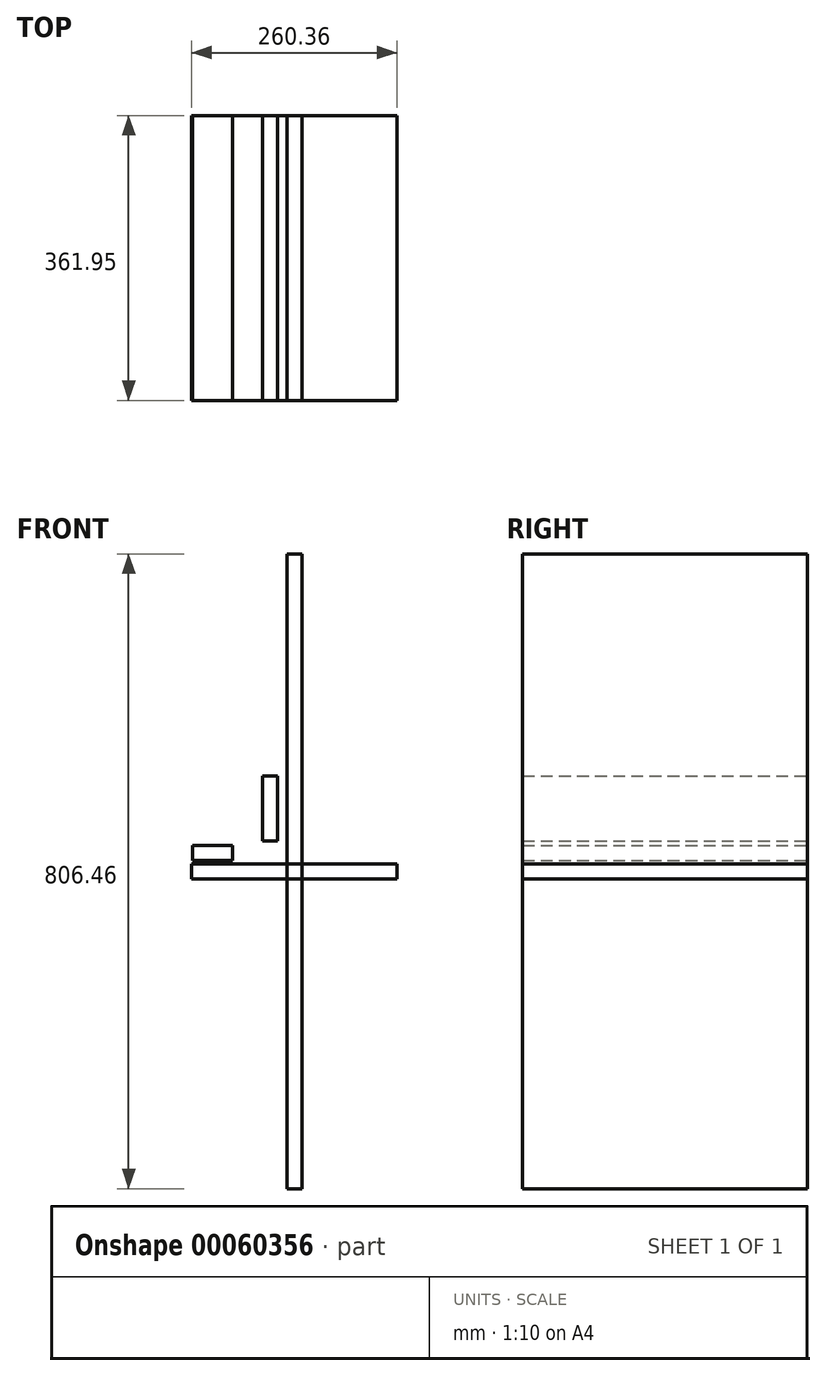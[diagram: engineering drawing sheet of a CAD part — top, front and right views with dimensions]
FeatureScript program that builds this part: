
annotation { "Feature Type Name" : "Feature", "Feature Type Description" : "" }
export const myFeature = defineFeature(function(context is Context, id is Id, definition is map)
    precondition{}
    {
        {
            var Q0;
            Q0=qCreatedBy(makeId("Front.planeOp"),FACE);
            var sketch = newSketch(context, id + "F0", { "sketchPlane" : qUnion([Q0])});
            skLineSegment(sketch, "E0.rect.bottom", {"start": v(9.52, -403.23) * mm, "end": v(-9.53, -403.23) * mm});
            skLineSegment(sketch, "E0.rect.top", {"start": v(9.53, 403.23) * mm, "end": v(-9.52, 403.23) * mm});
            skLineSegment(sketch, "E0.rect.left", {"start": v(9.52, -403.23) * mm, "end": v(9.53, 403.23) * mm});
            skLineSegment(sketch, "E0.rect.right", {"start": v(-9.53, -403.23) * mm, "end": v(-9.52, 403.23) * mm});
            skPoint(sketch, "E0.rect.middle", {"position": v(0, 0) * mm});
            skSolve(sketch);
        }
        {
            var Q0;
            Q0=makeQuery(id+"F0.imprint","IMPRINT",FACE,{"disambiguationData":[TD([[makeQuery(id+"F0.imprint","IMPRINT",EDGE,{"derivedFrom":sQuery(id+"F0.wireOp",EDGE,"E0.rect.bottom")}),-1.0]])]});
            extrude(context, id + "F1", {"entities" : qUnion([Q0]), "depth" : 361.95 * mm});
        }
        {
            var Q0;
            Q0=qCreatedBy(makeId("Front.planeOp"),FACE);
            var sketch = newSketch(context, id + "F2", { "sketchPlane" : qUnion([Q0])});
            skLineSegment(sketch, "E1.rect.bottom", {"start": v(130.18, -9.53) * mm, "end": v(-130.18, -9.53) * mm});
            skLineSegment(sketch, "E1.rect.top", {"start": v(130.18, 9.53) * mm, "end": v(-130.18, 9.53) * mm});
            skLineSegment(sketch, "E1.rect.left", {"start": v(130.18, -9.53) * mm, "end": v(130.18, 9.52) * mm});
            skLineSegment(sketch, "E1.rect.right", {"start": v(-130.18, -9.53) * mm, "end": v(-130.18, 9.52) * mm});
            skPoint(sketch, "E1.rect.middle", {"position": v(0, 0) * mm});
            skSolve(sketch);
        }
        {
            var Q0;
            Q0=makeQuery(id+"F2.imprint","IMPRINT",FACE,{"disambiguationData":[TD([[makeQuery(id+"F2.imprint","IMPRINT",EDGE,{"derivedFrom":sQuery(id+"F2.wireOp",EDGE,"E1.rect.bottom")}),-1.0]])]});
            extrude(context, id + "F3", {"entities" : qUnion([Q0]), "depth" : 361.95 * mm});
        }
        {
            var Q0;
            Q0=qCreatedBy(makeId("Front.planeOp"),FACE);
            var sketch = newSketch(context, id + "F4", { "sketchPlane" : qUnion([Q0])});
            skLineSegment(sketch, "E2.bottom", {"start": v(-129.05, 13.5) * mm, "end": v(-78.25, 13.5) * mm});
            skLineSegment(sketch, "E2.top", {"start": v(-129.05, 32.55) * mm, "end": v(-78.25, 32.55) * mm});
            skLineSegment(sketch, "E2.left", {"start": v(-129.05, 13.5) * mm, "end": v(-129.05, 32.55) * mm});
            skLineSegment(sketch, "E2.right", {"start": v(-78.25, 13.5) * mm, "end": v(-78.25, 32.55) * mm});
            skSolve(sketch);
        }
        {
            var Q0;
            Q0=makeQuery(id+"F4.imprint","IMPRINT",FACE,{"disambiguationData":[TD([[makeQuery(id+"F4.imprint","IMPRINT",EDGE,{"derivedFrom":sQuery(id+"F4.wireOp",EDGE,"E2.bottom")}),1.0]])]});
            extrude(context, id + "F5", {"entities" : qUnion([Q0]), "depth" : 361.95 * mm});
        }
        {
            var Q0;
            Q0=qCreatedBy(makeId("Front.planeOp"),FACE);
            var sketch = newSketch(context, id + "F6", { "sketchPlane" : qUnion([Q0])});
            skLineSegment(sketch, "E3.bottom", {"start": v(-40.1, 121.15) * mm, "end": v(-21.05, 121.15) * mm});
            skLineSegment(sketch, "E3.top", {"start": v(-40.1, 38.6) * mm, "end": v(-21.05, 38.6) * mm});
            skLineSegment(sketch, "E3.left", {"start": v(-40.1, 121.15) * mm, "end": v(-40.1, 38.6) * mm});
            skLineSegment(sketch, "E3.right", {"start": v(-21.05, 121.15) * mm, "end": v(-21.05, 38.6) * mm});
            skSolve(sketch);
        }
        {
            var Q0;
            Q0=makeQuery(id+"F6.imprint","IMPRINT",FACE,{"disambiguationData":[TD([[makeQuery(id+"F6.imprint","IMPRINT",EDGE,{"derivedFrom":sQuery(id+"F6.wireOp",EDGE,"E3.bottom")}),-1.0]])]});
            extrude(context, id + "F7", {"entities" : qUnion([Q0]), "depth" : 361.95 * mm});
        }
    });
